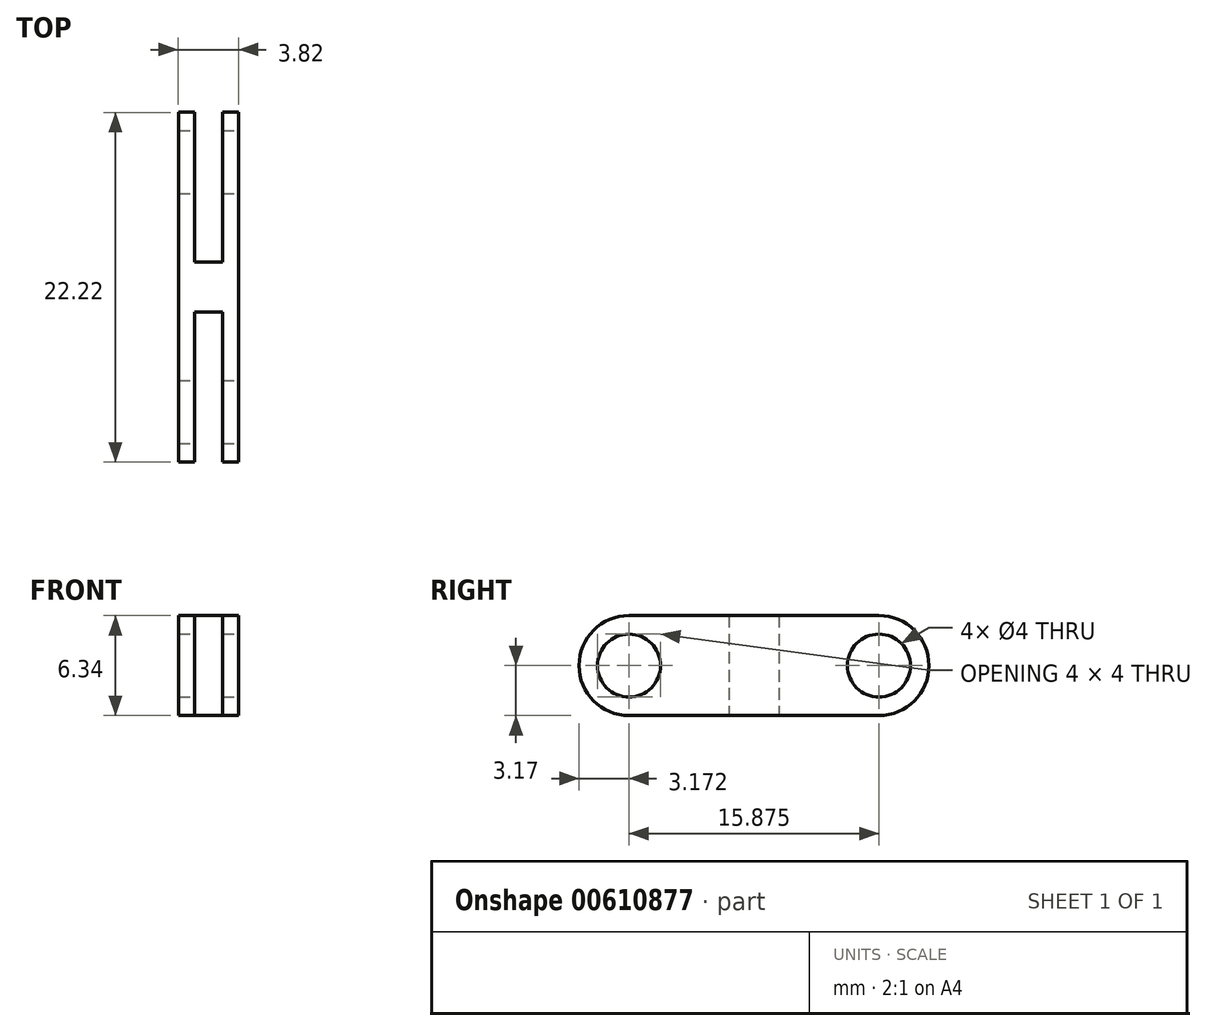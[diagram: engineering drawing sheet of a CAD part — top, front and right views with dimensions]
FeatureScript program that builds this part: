
annotation { "Feature Type Name" : "Feature", "Feature Type Description" : "" }
export const myFeature = defineFeature(function(context is Context, id is Id, definition is map)
    precondition{}
    {
        {
            var Q0;
            Q0=qCreatedBy(makeId("Right.planeOp"),FACE);
            var sketch = newSketch(context, id + "F0", { "sketchPlane" : qUnion([Q0])});
            skLineSegment(sketch, "E0.bottom", {"start": v(-1.59, 3.18) * mm, "end": v(1.59, 3.18) * mm});
            skLineSegment(sketch, "E0.top", {"start": v(-1.59, -3.18) * mm, "end": v(1.59, -3.18) * mm});
            skLineSegment(sketch, "E0.left", {"start": v(-1.59, 3.17) * mm, "end": v(-1.59, -3.17) * mm});
            skLineSegment(sketch, "E0.right", {"start": v(1.59, 3.18) * mm, "end": v(1.59, -3.18) * mm});
            skLineSegment(sketch, "E1", {"start": v(-1.59, 0) * mm, "end": v(0, 0) * mm});
            skLineSegment(sketch, "E2", {"start": v(0, 0) * mm, "end": v(1.59, 0) * mm});
            skSolve(sketch);
        }
        {
            var Q0;
            Q0 = qSketchRegion(id + "F0", true);
            extrude(context, id + "F1", {"entities" : qUnion([Q0]), "endBound" : BoundingType.SYMMETRIC, "depth" : 1.78 * mm, "offsetDistance" : 25.4 * mm});
        }
        {
            var Q0;
            Q0=makeQuery(id+"F1.opExtrude","SWEPT_FACE",FACE,{"disambiguationData":[OSD([sQuery(id+"F0.wireOp",EDGE,"E0.top")])]});
            var sketch = newSketch(context, id + "F2", { "sketchPlane" : qUnion([Q0])});
            skLineSegment(sketch, "E3", {"start": v(1.9, 0) * mm, "end": v(1.9, 11.11) * mm});
            skLineSegment(sketch, "E4", {"start": v(1.9, 11.11) * mm, "end": v(0.89, 11.11) * mm});
            skLineSegment(sketch, "E5", {"start": v(0.89, 11.11) * mm, "end": v(0.89, 1.59) * mm});
            skLineSegment(sketch, "E6", {"start": v(1.9, 0) * mm, "end": v(0.89, 0) * mm});
            skLineSegment(sketch, "E7", {"start": v(0.89, 0) * mm, "end": v(0, 0) * mm});
            skPoint(sketch, "E7.endSnap0", {"position": v(0, 1.59) * mm});
            skLineSegment(sketch, "E8", {"start": v(0, 1.59) * mm, "end": v(0, 0) * mm, "construction": true});
            skLineSegment(sketch, "E9.MirrorCS", {"start": v(-0.89, 11.11) * mm, "end": v(-0.89, 1.59) * mm});
            skLineSegment(sketch, "E10.MirrorCS", {"start": v(-1.9, 11.11) * mm, "end": v(-0.89, 11.11) * mm});
            skLineSegment(sketch, "E11.MirrorCS", {"start": v(-1.9, 0) * mm, "end": v(-1.9, 11.11) * mm});
            skLineSegment(sketch, "E12.MirrorCS", {"start": v(-1.9, 0) * mm, "end": v(-0.89, 0) * mm});
            skLineSegment(sketch, "E13.MirrorCS", {"start": v(-0.89, 0) * mm, "end": v(0, 0) * mm});
            skLineSegment(sketch, "E14", {"start": v(0.89, 1.59) * mm, "end": v(-0.89, 1.59) * mm});
            skLineSegment(sketch, "E15", {"start": v(-0.89, 0) * mm, "end": v(0.89, 0) * mm, "construction": true});
            skLineSegment(sketch, "E16.MirrorCS", {"start": v(1.9, 0) * mm, "end": v(1.9, -11.11) * mm});
            skLineSegment(sketch, "E17.MirrorCS", {"start": v(1.9, -11.11) * mm, "end": v(0.89, -11.11) * mm});
            skLineSegment(sketch, "E18.MirrorCS", {"start": v(0.89, -11.11) * mm, "end": v(0.89, -1.59) * mm});
            skLineSegment(sketch, "E19.MirrorCS", {"start": v(0.89, -1.59) * mm, "end": v(-0.89, -1.59) * mm});
            skLineSegment(sketch, "E20.MirrorCS", {"start": v(-0.89, -11.11) * mm, "end": v(-0.89, -1.59) * mm});
            skLineSegment(sketch, "E21.MirrorCS", {"start": v(-1.9, -11.11) * mm, "end": v(-0.89, -11.11) * mm});
            skLineSegment(sketch, "E22.MirrorCS", {"start": v(-1.9, 0) * mm, "end": v(-1.9, -11.11) * mm});
            skSolve(sketch);
        }
        {
            var Q0;
            Q0 = qSketchRegion(id + "F2", true);
            var Q1;
            Q1=makeQuery(id+"F1.opExtrude","SWEPT_FACE",FACE,{"disambiguationData":[OSD([sQuery(id+"F0.wireOp",EDGE,"E0.bottom")])]});
            extrude(context, id + "F3", {"entities" : qUnion([Q0]), "operationType" : NewBodyOperationType.ADD, "oppositeDirection" : true, "depth" : 6.35 * mm, "endBoundEntityFace" : qUnion([Q1]), "offsetDistance" : 25.4 * mm});
        }
        {
            var Q0;
            Q0=makeQuery(id+"F3.opExtrude","CAP_EDGE",EDGE,{"disambiguationData":[OSD([sQuery(id+"F2.wireOp",EDGE,"E4")])],"isStart":false});
            var Q1;
            Q1=makeQuery(id+"F3.opExtrude","CAP_EDGE",EDGE,{"disambiguationData":[OSD([sQuery(id+"F2.wireOp",EDGE,"E10.MirrorCS")])],"isStart":false});
            var Q2;
            Q2=makeQuery(id+"F3.opExtrude","CAP_EDGE",EDGE,{"disambiguationData":[OSD([sQuery(id+"F2.wireOp",EDGE,"E4")])],"isStart":true});
            var Q3;
            Q3=makeQuery(id+"F3.opExtrude","CAP_EDGE",EDGE,{"disambiguationData":[OSD([sQuery(id+"F2.wireOp",EDGE,"E10.MirrorCS")])],"isStart":true});
            var Q4;
            Q4=makeQuery(id+"F3.opExtrude","CAP_EDGE",EDGE,{"disambiguationData":[OSD([sQuery(id+"F2.wireOp",EDGE,"cb0f368e-af39-4470-a87c-ad9c8fa8e8120.MirrorCS")])],"isStart":false});
            var Q5;
            Q5=makeQuery(id+"F3.opExtrude","CAP_EDGE",EDGE,{"disambiguationData":[OSD([sQuery(id+"F2.wireOp",EDGE,"815dea8a-edc9-4474-8588-b6b1203f55720.MirrorCS")])],"isStart":false});
            var Q6;
            Q6=makeQuery(id+"F3.opExtrude","CAP_EDGE",EDGE,{"disambiguationData":[OSD([sQuery(id+"F2.wireOp",EDGE,"cb0f368e-af39-4470-a87c-ad9c8fa8e8120.MirrorCS")])],"isStart":true});
            var Q7;
            Q7=makeQuery(id+"F3.opExtrude","CAP_EDGE",EDGE,{"disambiguationData":[OSD([sQuery(id+"F2.wireOp",EDGE,"815dea8a-edc9-4474-8588-b6b1203f55720.MirrorCS")])],"isStart":true});
            var Q8;
            Q8=makeQuery(id+"F3.opExtrude","CAP_EDGE",EDGE,{"disambiguationData":[OSD([sQuery(id+"F2.wireOp",EDGE,"E21.MirrorCS")])],"isStart":true});
            var Q9;
            Q9=makeQuery(id+"F3.opExtrude","CAP_EDGE",EDGE,{"disambiguationData":[OSD([sQuery(id+"F2.wireOp",EDGE,"E17.MirrorCS")])],"isStart":true});
            var Q10;
            Q10=makeQuery(id+"F3.opExtrude","CAP_EDGE",EDGE,{"disambiguationData":[OSD([sQuery(id+"F2.wireOp",EDGE,"E17.MirrorCS")])],"isStart":false});
            var Q11;
            Q11=makeQuery(id+"F3.opExtrude","CAP_EDGE",EDGE,{"disambiguationData":[OSD([sQuery(id+"F2.wireOp",EDGE,"E21.MirrorCS")])],"isStart":false});
            fillet(context, id + "F4", {"entities" : qUnion([Q0, Q1, Q2, Q3, Q4, Q5, Q6, Q7, Q8, Q9, Q10, Q11]), "radius" : 3.17 * mm, "tangentPropagation" : true, "allowEdgeOverflow" : false});
        }
        {
            var Q0;
            Q0=makeQuery(id+"F3.opExtrude","SWEPT_FACE",FACE,{"disambiguationData":[OSD([sQuery(id+"F2.wireOp",EDGE,"E3")])]});
            var sketch = newSketch(context, id + "F5", { "sketchPlane" : qUnion([Q0])});
            skPoint(sketch, "E23", {"position": v(-7.94, 0) * mm});
            skSolve(sketch);
        }
        {
            var Q0;
            Q0=makeQuery(id+"F3.opExtrude","SWEPT_FACE",FACE,{"disambiguationData":[OSD([sQuery(id+"F2.wireOp",EDGE,"E16.MirrorCS")])]});
            var sketch = newSketch(context, id + "F6", { "sketchPlane" : qUnion([Q0])});
            skPoint(sketch, "E24", {"position": v(7.94, 0) * mm});
            skSolve(sketch);
        }
        {
            var Q0;
            Q0=sQuery(id+"F5.wireOp",VERTEX,"E23");
            var Q1;
            Q1=sQuery(id+"F6.wireOp",VERTEX,"E24");
            var Q2;
            Q2=makeQuery(id+"F1.opExtrude","SWEPT_BODY",BODY,{"disambiguationData":[OSD([sQuery(id+"F0.wireOp",EDGE,"E0.bottom"),sQuery(id+"F0.wireOp",EDGE,"E0.top"),sQuery(id+"F0.wireOp",EDGE,"E0.left"),sQuery(id+"F0.wireOp",EDGE,"E0.right")])]});
            hole(context, id + "F7", {"style" : HoleStyle.SIMPLE, "endStyle" : HoleEndStyle.THROUGH, "holeDiameter" : 4 * mm, "majorDiameter" : 6.35 * mm, "isTappedThrough" : true, "tappedDepth" : 12.7 * mm, "tapClearance" : 3, "locations" : qUnion([Q0, Q1]), "scope" : qUnion([Q2])});
        }
    });
